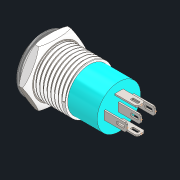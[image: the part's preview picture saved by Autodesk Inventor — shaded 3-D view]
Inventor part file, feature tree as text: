
AUTODESK INVENTOR PART (.ipt)
format: ipt  version: 2022 (Build 260153000, 153)  size: 499,712 bytes
history: mixed  units: in
note: dims shown in document units (in); Inventor stores cm internally (conversion verified against a paired STEP export)
features: other x6, revolve x1, imported_body x1
ambient origin geometry x8: Origin, YZ Plane, XZ Plane, XY Plane, X Axis, Y Axis, Z Axis, Center Point
bodies: Solid1 (imported_parasolid), Solid2 (imported_parasolid)
feature tree (8):
  other  "Work Point1"
  other  "Work Point2"
  other  "Work Point3"
  other  "Work Point4"
  other  "Work Point5"
  revolve  "Revolve2"  [1 undecoded]
  other  "Cut-Extrude3"
  imported_body  NMx_Import_Brep_tag  [imported B-rep: ~10 faces, bbox_mm=[0.0, 0.0, 0.0]]
note: 1 required parameter value undecoded (feature->parameter linkage not recoverable at this tier; creation-order binding heuristic only, values carry confidence <= 0.55)
